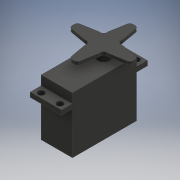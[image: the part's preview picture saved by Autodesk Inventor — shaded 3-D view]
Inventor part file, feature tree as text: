
AUTODESK INVENTOR PART (.ipt)
format: ipt  version: 2018 (Build 220112000, 112)  size: 217,600 bytes
history: native  units: mm
features: extrude x5, sketch x5
ambient origin geometry x8: Origin, YZ Plane, XZ Plane, XY Plane, X Axis, Y Axis, Z Axis, Center Point
bodies: Solid1 (feature_tree)
feature tree (10):
  extrude  "Extrusion1"  Depth=41.0mm
  extrude  "Extrusion2"  Depth=20.0mm
  extrude  "Extrusion3"  Depth=4.0mm
  extrude  "Extrusion4"  Depth=4.0mm
  extrude  "Extrusion5"  Depth=4.0mm
  sketch  "Sketch1"  dims[d0=20.0mm d1=41.0mm]
  sketch  "Sketch2"  dims[d2=27.0mm d3=0.0mm d4=20.0mm]
  sketch  "Sketch3"  dims[d5=55.0mm d6=4.0mm]
  sketch  "Sketch4"  dims[d7=4.0mm d8=4.0mm]
  sketch  "Sketch5"  dims[d9=4.0mm d10=4.0mm d11=4.0mm d12=4.0mm d13=4.0mm d14=4.0mm d15=4.0mm d16=4.0mm d17=3.0mm d18=0.0mm d19=20.0mm d20=41.0mm d21=6.0mm d22=0.0mm d23=18.0mm d24=8.0mm d25=8.0mm d26=0.0mm d27=39.0mm d28=9.0mm d29=9.0mm d30=39.0mm d31=29.5mm d32=49.5mm d33=2.0mm d34=12.0mm d35=1.745329mm d36=12.0mm d37=1.745329mm d38=12.0mm d39=1.745329mm d40=12.0mm d41=1.745329mm d42=12.0mm d43=1.745329mm d44=12.0mm d45=1.745329mm d46=12.0mm d47=1.745329mm d48=12.0mm d49=1.745329mm d50=2.0mm d51=2.0mm d52=2.0mm d53=0.0mm]
